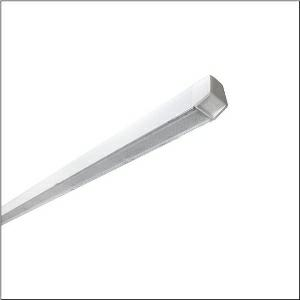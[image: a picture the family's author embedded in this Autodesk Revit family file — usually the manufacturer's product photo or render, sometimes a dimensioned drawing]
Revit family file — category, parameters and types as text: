
# Revit family: licross_r__21_recessed_ho_52ul1edv4k5r00s_c975
name_source: partatom
category: Lighting Fixtures
units: mm (PartAtom-declared; Revit-internal decimal feet)

## family parameters
Cut with Voids When Loaded = No
Host = Face
Light Source = No
Part Type = Normal
Room Calculation Point = No
Round Connector Dimension = Use Diameter
Shared = No

## types (1)
- --- (1 x LED, 19890 lm, 121.7 W, 4000K)
    Apparent Load = 122 VA
    CIE Flux Codes = 85 95 99 100 100
    Color Rendering = 80
    Color Temperature = 4000K
    Default Elevation = 1800 mm
    Description = Licross® 21 Recessed HO, single luminaire, primary optical cover: cover, of PMMA, light emission: direct distribution, installation type: slip-in mounting, LED, rated luminous flux: 19.890lm, luminous efficacy: 163lm/W, light colour: 840, colour temperature: 4000K, control gear: ECG DALI, with terminal, 5-pole, max. 2.5mm², mains connection: 230V, AC, 50/60Hz, rated input power: 122W, Licross® LED insert, of sheet steel, galvanised, coil coated, white, length: 2.327mm, width: 70mm, height: 71mm, end cap, of PC, white, mounting rail, of sheet steel, galvanised, white, protection rating (complete): IP20, insulation class (complete): insulation class I (protective earthing), certification: CE, ENEC, VDE, UKCA, impact resistance: IK06, permissible operating ambient temperature: -35..+30°C, corresponds to IFS (International Featured Standards) requirements for safety and quality in the food industry, reducing of maximum allowable ambient temperature of 5°C with ceiling mounting, LABS conformity tested according to VDMA 24364:2018-05, packaging unit: 1 piece
    Height = 58 mm
    Lamp = 1 x LED
    Lamp Light Flux = 19890 lm
    Lamp Power = 121.7 W
    Lamp count = 1
    Length = 2250 mm
    Luminous efficacy = 163 lm/W
    Manufacturer = Siteco
    ModVariant = No
    Model = 52UL1EDV4K5R00S
    Mounting Place = Ceiling
    Mounting Type = Pendant
    Number of Poles = 1
    OnlyDefault = Yes
    Power Factor = 1
    Product Name = Licross® 21 Recessed HO
    Product group = single luminaire
    ProductGroupID = 909
    Protection Class = Protection class I
    Protection Degree = IP 20
    RLX_Detail_Level = 1
    RlxData = <blob elided: 31917 chars, md5=6991a111>
    Socket = socket
    Standby Power = 0 W
    System Light Flux = 19889 lm
    System Power = 122 W
    Type Comments = factory setting: luminous flux: 100 % | dim-lin: 254 | 490 mA
    Type Image = l_1006979.jpg
    URL = http://relux.com
    VarID = @adj_092755
    Voltage = 0 V
    Weight = 0.00 kg
    Width = 66 mm

## geometry (parser evidence)
native form markers: Blend x4, Sweep x9
no freeform markers — native parametric forms only
